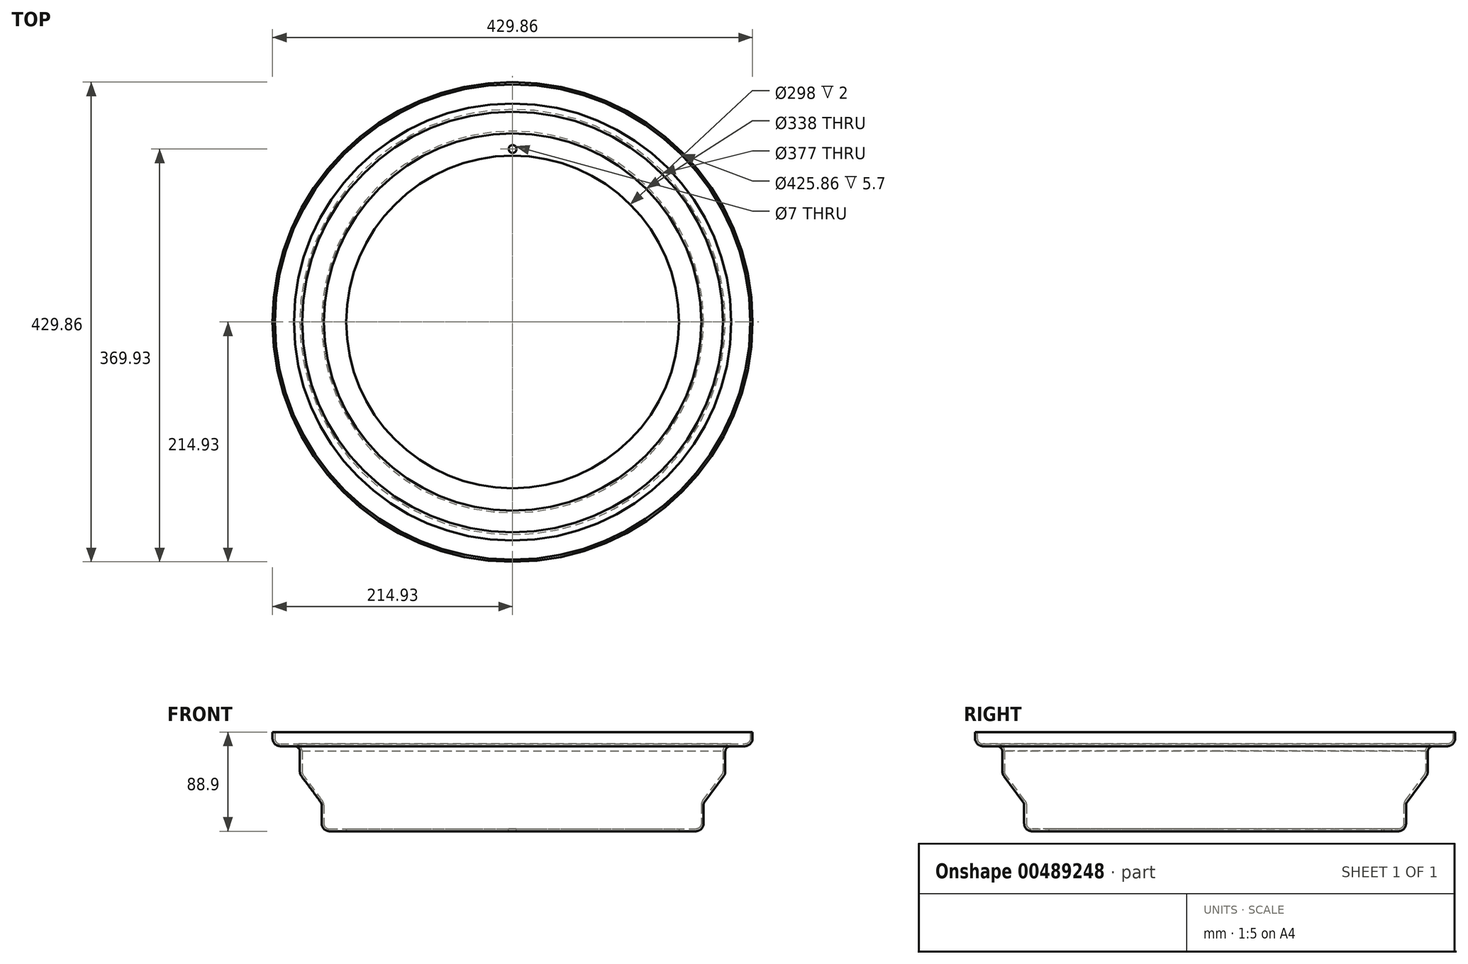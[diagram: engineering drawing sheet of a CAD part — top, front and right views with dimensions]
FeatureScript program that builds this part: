
annotation { "Feature Type Name" : "Feature", "Feature Type Description" : "" }
export const myFeature = defineFeature(function(context is Context, id is Id, definition is map)
    precondition{}
    {
        {
            var Q0;
            Q0=qCreatedBy(makeId("Front.planeOp"),FACE);
            var sketch = newSketch(context, id + "F0", { "sketchPlane" : qUnion([Q0])});
            skLineSegment(sketch, "E0", {"start": v(-149, 0) * mm, "end": v(-164, 0) * mm});
            skLineSegment(sketch, "E1", {"start": v(-149, 0) * mm, "end": v(-149, 2) * mm});
            skLineSegment(sketch, "E2", {"start": v(-149, 2) * mm, "end": v(-164, 2) * mm});
            skLineSegment(sketch, "E3", {"start": v(-212.93, 83.2) * mm, "end": v(-212.93, 88.9) * mm});
            skLineSegment(sketch, "E4", {"start": v(-212.93, 88.9) * mm, "end": v(-214.93, 88.9) * mm});
            skLineSegment(sketch, "E5", {"start": v(-214.93, 88.9) * mm, "end": v(-214.93, 83.2) * mm});
            skLineSegment(sketch, "E6", {"start": v(-207.93, 76.2) * mm, "end": v(-195.5, 76.2) * mm});
            skLineSegment(sketch, "E7", {"start": v(-190.5, 71.2) * mm, "end": v(-190.5, 53.52) * mm});
            skLineSegment(sketch, "E8", {"start": v(0, 0) * mm, "end": v(0, 45.18) * mm, "construction": true});
            skPoint(sketch, "E9.visualSharp", {"position": v(-188.5, 78.2) * mm});
            skArc(sketch, "E9.filletArc", {"start": v(-188.5, 71.86) * mm, "mid": v(-190.89, 76.5) * mm, "end": v(-195.83, 78.2) * mm});
            skPoint(sketch, "E10.visualSharp", {"position": v(-190.5, 76.2) * mm});
            skArc(sketch, "E10.filletArc", {"start": v(-190.5, 71.2) * mm, "mid": v(-191.96, 74.74) * mm, "end": v(-195.5, 76.2) * mm});
            skPoint(sketch, "E11.visualSharp", {"position": v(-212.93, 78.66) * mm});
            skArc(sketch, "E11.filletArc", {"start": v(-212.93, 83.2) * mm, "mid": v(-211.47, 79.66) * mm, "end": v(-207.93, 78.2) * mm});
            skPoint(sketch, "E12.visualSharp", {"position": v(-214.93, 76.2) * mm});
            skArc(sketch, "E12.filletArc", {"start": v(-214.93, 83.2) * mm, "mid": v(-212.88, 78.25) * mm, "end": v(-207.93, 76.2) * mm});
            skLineSegment(sketch, "E13", {"start": v(-207.93, 78.2) * mm, "end": v(-195.83, 78.2) * mm});
            skLineSegment(sketch, "E14", {"start": v(-188.5, 71.86) * mm, "end": v(-188.5, 53.52) * mm});
            skLineSegment(sketch, "E15", {"start": v(-169, 7) * mm, "end": v(-169, 23.34) * mm});
            skPoint(sketch, "E16.visualSharp", {"position": v(-169, 2) * mm});
            skArc(sketch, "E16.filletArc", {"start": v(-169, 7) * mm, "mid": v(-167.54, 3.46) * mm, "end": v(-164, 2) * mm});
            skArc(sketch, "E17", {"start": v(-171, 7) * mm, "mid": v(-168.95, 2.05) * mm, "end": v(-164, 0) * mm});
            skLineSegment(sketch, "E18", {"start": v(-171, 7) * mm, "end": v(-171, 23.34) * mm});
            skLineSegment(sketch, "E19", {"start": v(-187.51, 50.53) * mm, "end": v(-170.38, 27.52) * mm});
            skLineSegment(sketch, "E20", {"start": v(-171.99, 26.33) * mm, "end": v(-189.12, 49.34) * mm});
            skPoint(sketch, "E21.visualSharp", {"position": v(-188.5, 51.86) * mm});
            skArc(sketch, "E21.filletArc", {"start": v(-188.5, 53.52) * mm, "mid": v(-188.25, 51.95) * mm, "end": v(-187.51, 50.53) * mm});
            skPoint(sketch, "E22.visualSharp", {"position": v(-171, 25) * mm});
            skArc(sketch, "E22.filletArc", {"start": v(-171, 23.34) * mm, "mid": v(-171.25, 24.92) * mm, "end": v(-171.99, 26.33) * mm});
            skPoint(sketch, "E23.visualSharp", {"position": v(-190.5, 51.2) * mm});
            skArc(sketch, "E23.filletArc", {"start": v(-190.5, 53.52) * mm, "mid": v(-190.14, 51.32) * mm, "end": v(-189.12, 49.34) * mm});
            skPoint(sketch, "E24.visualSharp", {"position": v(-169, 25.66) * mm});
            skArc(sketch, "E24.filletArc", {"start": v(-169, 23.34) * mm, "mid": v(-169.36, 25.54) * mm, "end": v(-170.38, 27.52) * mm});
            skSolve(sketch);
        }
        {
            var Q0;
            Q0=makeQuery(id+"F0.imprint","IMPRINT",FACE,{"disambiguationData":[TD([[makeQuery(id+"F0.imprint","IMPRINT",EDGE,{"derivedFrom":sQuery(id+"F0.wireOp",EDGE,"E0")}),-1.0]])]});
            var Q1;
            Q1=sQuery(id+"F0.wireOp",EDGE,"E8");
            revolve(context, id + "F1", {"entities" : qUnion([Q0]), "axis" : qUnion([Q1]), "revolveType" : RevolveType.FULL});
        }
        {
            var Q0;
            Q0=makeQuery(id+"F1.opRevolve","SWEPT_FACE",FACE,{"disambiguationData":[OSD([sQuery(id+"F0.wireOp",EDGE,"E2")])]});
            var sketch = newSketch(context, id + "F2", { "sketchPlane" : qUnion([Q0])});
            skLineSegment(sketch, "E25", {"start": v(0, 0) * mm, "end": v(0, 155) * mm, "construction": true});
            skCircle(sketch, "E26", {"center": v(0, 155) * mm, "radius": 3.5 * mm});
            skSolve(sketch);
        }
        {
            var Q0;
            Q0=makeQuery(id+"F2.imprint","IMPRINT",FACE,{"disambiguationData":[TD([[makeQuery(id+"F2.imprint","IMPRINT",EDGE,{"derivedFrom":sQuery(id+"F2.wireOp",EDGE,"E26")}),1.0]])]});
            extrude(context, id + "F3", {"entities" : qUnion([Q0]), "operationType" : NewBodyOperationType.REMOVE, "endBound" : BoundingType.THROUGH_ALL, "oppositeDirection" : true, "depth" : 25 * mm});
        }
    });
